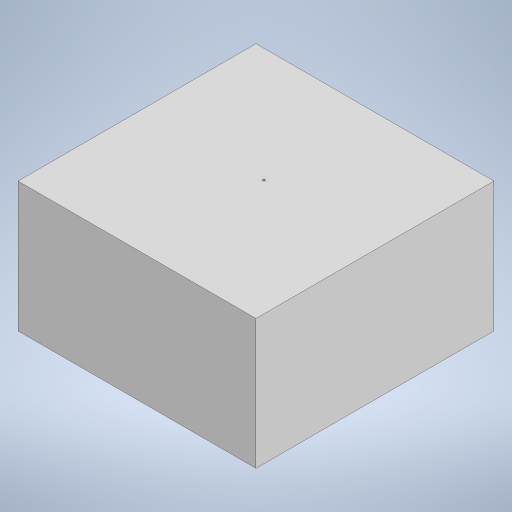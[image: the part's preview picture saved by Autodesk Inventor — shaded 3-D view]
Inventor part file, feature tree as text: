
AUTODESK INVENTOR PART (.ipt)
format: ipt  version: 2023 (Build 270158000, 158)  size: 169,984 bytes
history: native  units: in
note: dims shown in document units (in); Inventor stores cm internally (conversion verified against a paired STEP export)
features: sketch x2, extrude x1, hole x1
ambient origin geometry x8: Origin, YZ Plane, XZ Plane, XY Plane, X Axis, Y Axis, Z Axis, Center Point
bodies: Solide1 (feature_tree)
feature tree (4):
  extrude  "Extrusion1"  Depth=21.6535in
  hole  "Perçage1"  [1 undecoded]
  sketch  "Esquisse1"
  sketch  "Esquisse2"
note: 1 required parameter value undecoded (feature->parameter linkage not recoverable at this tier; creation-order binding heuristic only, values carry confidence <= 0.55)
